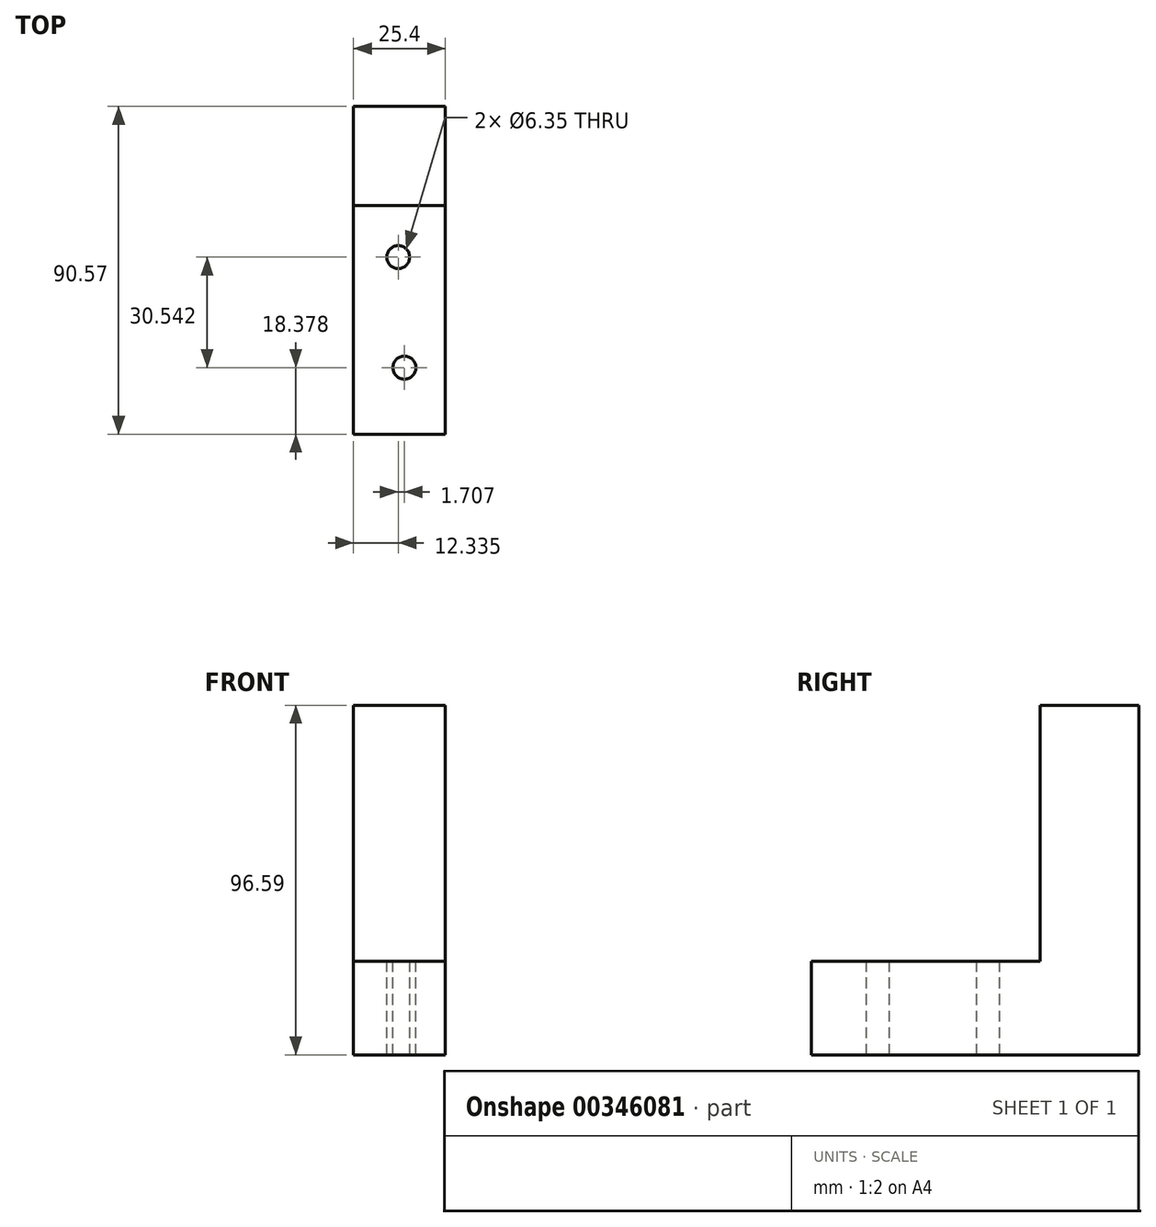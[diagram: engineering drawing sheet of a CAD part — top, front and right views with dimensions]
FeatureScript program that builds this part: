
annotation { "Feature Type Name" : "Feature", "Feature Type Description" : "" }
export const myFeature = defineFeature(function(context is Context, id is Id, definition is map)
    precondition{}
    {
        {
            var Q0;
            Q0=qCreatedBy(makeId("Right.planeOp"),FACE);
            var sketch = newSketch(context, id + "F0", { "sketchPlane" : qUnion([Q0])});
            skLineSegment(sketch, "E0", {"start": v(-48.92, -31.36) * mm, "end": v(14.3, -31.36) * mm});
            skLineSegment(sketch, "E1", {"start": v(14.3, -31.36) * mm, "end": v(14.3, 39.39) * mm});
            skLineSegment(sketch, "E2", {"start": v(14.3, 39.39) * mm, "end": v(41.65, 39.39) * mm});
            skLineSegment(sketch, "E3", {"start": v(41.65, 39.39) * mm, "end": v(41.65, -57.2) * mm});
            skLineSegment(sketch, "E4", {"start": v(41.65, -57.2) * mm, "end": v(-48.92, -57.2) * mm});
            skLineSegment(sketch, "E5", {"start": v(-48.92, -57.2) * mm, "end": v(-48.92, -31.36) * mm});
            skLineSegment(sketch, "E6", {"start": v(1153.07, -180.86) * mm, "end": v(1149.9, -206.3) * mm});
            skLineSegment(sketch, "E7", {"start": v(1153.07, -180.86) * mm, "end": v(1153.07, -172.37) * mm});
            skSolve(sketch);
        }
        {
            var Q0;
            Q0=makeQuery(id+"F0.imprint","IMPRINT",FACE,{"disambiguationData":[TD([[makeQuery(id+"F0.imprint","IMPRINT",EDGE,{"derivedFrom":sQuery(id+"F0.wireOp",EDGE,"E0")}),-1.0]])]});
            var Q1;
            Q1 = qSketchRegion(id + "FFq7xxI6JaxFRbh_1", true);
            extrude(context, id + "F1", {"entities" : qUnion([Q0, Q1]), "depth" : 25.4 * mm});
        }
        {
            var Q0;
            Q0=makeQuery(id+"F1.opExtrude","SWEPT_FACE",FACE,{"disambiguationData":[OSD([sQuery(id+"F0.wireOp",EDGE,"E0")])]});
            var sketch = newSketch(context, id + "F2", { "sketchPlane" : qUnion([Q0])});
            skCircle(sketch, "E8", {"center": v(14.04, -30.54) * mm, "radius": 6.46 * mm});
            skCircle(sketch, "E9", {"center": v(13.74, -2.87) * mm, "radius": 5.88 * mm});
            skSolve(sketch);
        }
        {
            var Q0;
            Q0=sQuery(id+"F2.wireOp",VERTEX,"E8.center");
            var Q1;
            Q1=makeQuery(id+"F1.opExtrude","SWEPT_BODY",BODY,{"disambiguationData":[OSD([sQuery(id+"F0.wireOp",EDGE,"E0"),sQuery(id+"F0.wireOp",EDGE,"E1"),sQuery(id+"F0.wireOp",EDGE,"E2"),sQuery(id+"F0.wireOp",EDGE,"E3"),sQuery(id+"F0.wireOp",EDGE,"E4"),sQuery(id+"F0.wireOp",EDGE,"E5")])]});
            hole(context, id + "F3", {"style" : HoleStyle.SIMPLE, "endStyle" : HoleEndStyle.THROUGH, "holeDiameter" : 6.35 * mm, "isTappedThrough" : true, "tappedDepth" : 12.7 * mm, "tapClearance" : 3, "locations" : qUnion([Q0]), "scope" : qUnion([Q1])});
        }
        {
            var Q0;
            Q0=makeQuery(id+"F1.opExtrude","SWEPT_FACE",FACE,{"disambiguationData":[OSD([sQuery(id+"F0.wireOp",EDGE,"E0")])]});
            var sketch = newSketch(context, id + "F4", { "sketchPlane" : qUnion([Q0])});
            skCircle(sketch, "E10", {"center": v(12.33, 0) * mm, "radius": 5.32 * mm});
            skSolve(sketch);
        }
        {
            var Q0;
            Q0=sQuery(id+"F4.wireOp",VERTEX,"E10.center");
            var Q1;
            Q1=makeQuery(id+"F1.opExtrude","SWEPT_BODY",BODY,{"disambiguationData":[OSD([sQuery(id+"F0.wireOp",EDGE,"E0"),sQuery(id+"F0.wireOp",EDGE,"E1"),sQuery(id+"F0.wireOp",EDGE,"E2"),sQuery(id+"F0.wireOp",EDGE,"E3"),sQuery(id+"F0.wireOp",EDGE,"E4"),sQuery(id+"F0.wireOp",EDGE,"E5")])]});
            hole(context, id + "F5", {"style" : HoleStyle.SIMPLE, "endStyle" : HoleEndStyle.THROUGH, "holeDiameter" : 6.35 * mm, "isTappedThrough" : true, "tappedDepth" : 12.7 * mm, "tapClearance" : 3, "locations" : qUnion([Q0]), "scope" : qUnion([Q1])});
        }
    });
